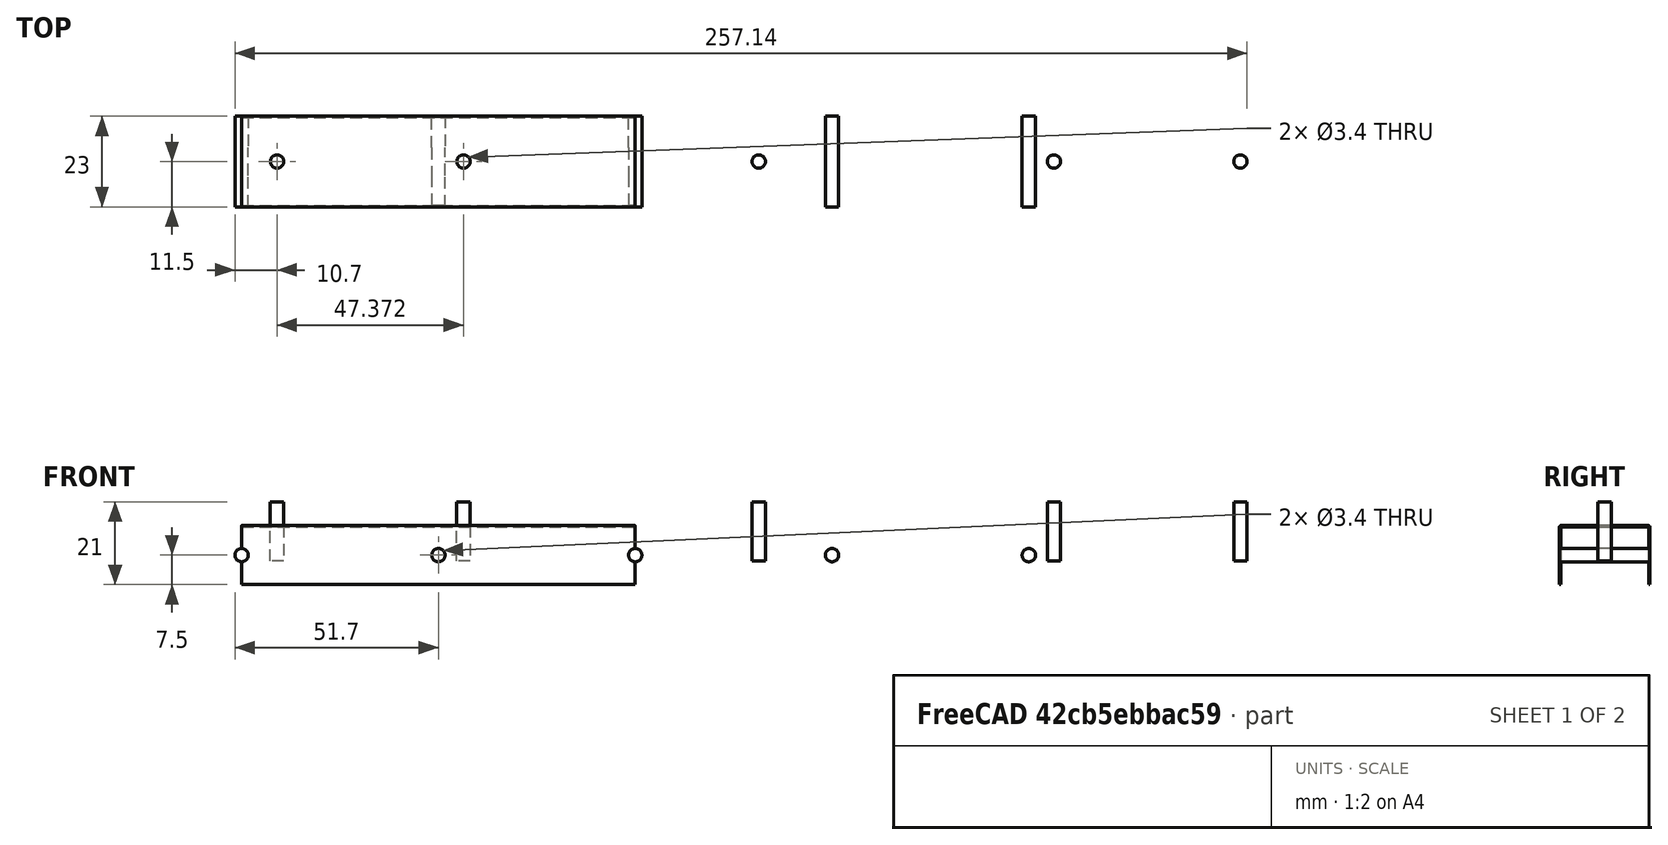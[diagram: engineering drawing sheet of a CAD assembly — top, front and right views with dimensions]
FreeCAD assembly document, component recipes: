
FREECAD ASSEMBLY — COMPONENT RECIPES ("composit_stand3_dropper_fix_fixture_model")

This assembly document has 2 components, labeled P0..P1 below (a component is one placed body or linked part). 2 of them carry a construction recipe — the FreeCAD feature program that regenerates the part from scratch, quoted from this document or its linked companion documents; the rest are supplied as boundary geometry only. No exploded tour is included for this assembly.
COMPONENT P0 — recipe-attached ("dropper_fix_fixture", modeled in this document).
Construction recipe (the document's own serialized feature program — sketch geometry with constraints, then the solid features built on it; lengths are millimeters unless a unit is written):

FEATURE [PartDesign::SubShapeBinder] Binder001
  BindCopyOnChange = 0
  BindMode = 0
  ClaimChildren = true
  Context = -> Body [Binder001.]
  Fuse = false
  MakeFace = true
  OffsetFill = false
  OffsetIntersection = false
  OffsetJoinType = 0
  OffsetOpenResult = false
  PartialLoad = false
  Placement = pos=(0,0,0) rot=(0.57735,0.57735,0.57735;2.0944rad)
  Relative = false
  Support = -> [Binder]
  _Version = 2
  expr: Placement = Support[0][0].Placement
FEATURE [PartDesign::FeaturePython] BaseBend  # WARN: FeaturePython — macro-defined, semantics opaque (R4)
  BendSide = 1
  BendSketch = -> Binder001
  MidPlane = false
  Reverse = false
  Suppressed = false
  length = 100
  radius = 0.1
  thickness = 0.3
FEATURE [PartDesign::Boolean] Boolean
  BaseFeature = -> BaseBend
  Group = -> [Fusion]
  Suppressed = false
  Type = 1
  UsePlacement = true
FEATURE [PartDesign::CoordinateSystem] Local_CS
  AttacherType = Attacher::AttachEngine3D
  AttachmentOffset = pos=(-50,0,0) rot=(0,0,1;0rad)
  AttachmentSupport = -> [XY_Plane]
  MapMode = 5
  Placement = pos=(-50,0,0) rot=(0,0,1;0rad)
  expr: .AttachmentOffset.Base.x = <<Placment>>.LinkedObject.Placement.Base.x
FEATURE [PartDesign::Body] Body  label="dropper_fix_fixture"
  AllowCompound = false
  Group = -> [Binder001,BaseBend,Boolean,Local_CS]
  Origin = -> Origin
  Tip = -> Boolean
COMPONENT P1 — recipe-attached ("hole_3.4mm", a linked part whose construction recipe lives in a companion FreeCAD document of the same project; that document's serialized recipe follows).
Construction recipe (the companion document, serialized — sketch geometry with constraints, then the solid features built on it; lengths are millimeters unless a unit is written):

FCSTD DOCUMENT  (FreeCAD 1.1R38827 (Git))
Label: composit_stand3_main
License: All rights reserved
LicenseURL: http://en.wikipedia.org/wiki/All_rights_reserved
objects: Part::Cylinder×2, Sketcher::SketchObject×1, Part::FeaturePython×1
note: 5 computed .brp shape members not serialized (recipe doc carries the construction recipe); baked Part::Feature solids carry a one-line shape summary decoded from their .brp

FEATURE [Sketcher::SketchObject] Sketch  label="main_sketch"
  ArcFitTolerance = 0
  FullyConstrained = true
  MakeInternals = false
  sketch-geometry (4):
    g0: LineSegment [constr] StartX=0 StartY=0 StartZ=0 EndX=8.37158 EndY=14.5 EndZ=0
    g1: LineSegment StartX=8.37158 StartY=14.5 StartZ=0 EndX=351.872 EndY=14.5 EndZ=0
    g2: LineSegment StartX=351.872 StartY=14.5 StartZ=0 EndX=351.872 EndY=0 EndZ=0
    g3: GeomPoint [constr] X=351.872 Y=-14.5 Z=0
  constraints (13):
    c: Coincident(g-1,g0)
    c: Horizontal(g1)
    c: Coincident(g1,g2)
    c: PointOnObject(g2,g-1)
    c: Vertical(g2)
    c: Angle(g0) = 1.0472
    c: DistanceX(g0,g1) = 343.5  'face_width'
    c: DistanceY(g3,g1) = 29  'end_width'
    c: Symmetric(g3,g1,g2)
    c: DistanceX(g0) = 8.37158  'x_face_offset'
    c: Coincident(g1,g0)
    c: Distance(g0) = 16.7432  'corner_distance'
    c: DistanceY(g0,g0) = 14.5
FEATURE [Part::FeaturePython] LinearArray  label="modules_placement_x"  # WARN: FeaturePython — macro-defined, semantics opaque (R4)
  Alignment = 0
  CellStart = A1
  Count = 2
  Dir = (1,0,0)
  DirIsDriven = true
  DistributionLaw = 0
  DrivenProperty = 1
  EndInclusive = true
  ExposePlacement = false
  GeneratorMode = 0
  MarkerShape = 1
  MarkerSize = 0
  NumElements = 2
  OrientMode = 1
  Placement = pos=(8.37158,14.5,0) rot=(0,0,1;0rad)
  Point = (0,0,0)
  PointIsDriven = true
  Reverse = false
  SpanEnd = 248
  SpanStart = 98
  Step = 150
  Type = lattice2LinearArray.LinearArray
  VSGVersion = 1
  Values = 98.0 | 248.0
  ValuesSource = 2
  isLattice = 1
  expr: .Placement.Base.x = <<main_sketch>>.Constraints.end_width / 2 / tan(60)
  expr: .Placement.Base.y = <<main_sketch>>.Constraints.end_width / 2
FEATURE [Part::Cylinder] Cylinder  label="hole_3.4mm"
  Angle = 360
  AttacherType = Attacher::AttachEngine3D
  FirstAngle = 0
  Height = 15
  Radius = 1.7
  SecondAngle = 0
FEATURE [Part::Cylinder] Cylinder001  label="hole_3.4mm_rev"
  Angle = 360
  AttacherType = Attacher::AttachEngine3D
  FirstAngle = 0
  Height = 15
  Placement = pos=(0,0,0) rot=(1,0,0;3.14159rad)
  Radius = 1.7
  SecondAngle = 0
PROVENANCE & LICENSES
A FreeCAD (.FCStd) document from a public repository crawl; recipes are the document's own serialized feature recipes (and, for linked parts, companion documents' recipes).
License: as declared in the source repository (recorded in the dataset sidecar).
